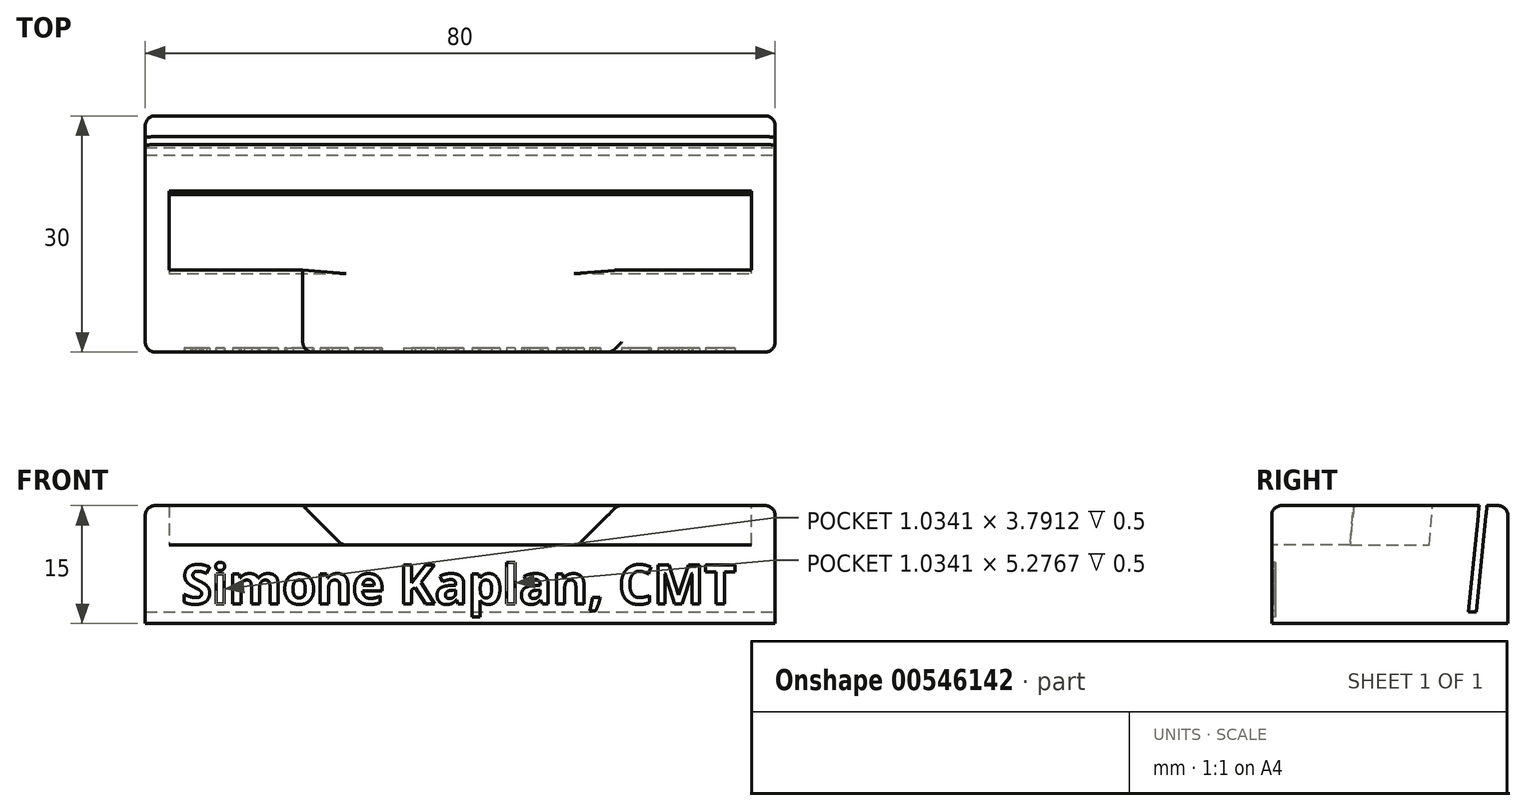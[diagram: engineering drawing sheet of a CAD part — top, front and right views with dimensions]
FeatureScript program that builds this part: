
annotation { "Feature Type Name" : "Feature", "Feature Type Description" : "" }
export const myFeature = defineFeature(function(context is Context, id is Id, definition is map)
    precondition{}
    {
        {
            var Q0;
            Q0=qCreatedBy(makeId("Right.planeOp"),FACE);
            var sketch = newSketch(context, id + "F0", { "sketchPlane" : qUnion([Q0])});
            skLineSegment(sketch, "E0.bottom", {"start": v(0, 0) * mm, "end": v(30, 0) * mm});
            skLineSegment(sketch, "E0.top", {"start": v(0, 15) * mm, "end": v(30, 15) * mm});
            skLineSegment(sketch, "E0.left", {"start": v(0, 0) * mm, "end": v(0, 15) * mm});
            skLineSegment(sketch, "E0.right", {"start": v(30, 0) * mm, "end": v(30, 15) * mm});
            skSolve(sketch);
        }
        {
            var Q0;
            Q0=qSketchRegion(id+"F0",true);
            extrude(context, id + "F1", {"entities" : qUnion([Q0]), "depth" : 80 * mm});
        }
        {
            var Q0;
            Q0=makeQuery(id+"F1.opExtrude","CAP_FACE",FACE,{"disambiguationData":[OSD([sQuery(id+"F0.wireOp",EDGE,"E0.bottom"),sQuery(id+"F0.wireOp",EDGE,"E0.top"),sQuery(id+"F0.wireOp",EDGE,"E0.left"),sQuery(id+"F0.wireOp",EDGE,"E0.right")])],"isStart":false});
            var sketch = newSketch(context, id + "F2", { "sketchPlane" : qUnion([Q0])});
            skLineSegment(sketch, "E1", {"start": v(10.42, 15) * mm, "end": v(9.98, 10) * mm});
            skLineSegment(sketch, "E2", {"start": v(9.98, 10) * mm, "end": v(20.02, 10) * mm});
            skLineSegment(sketch, "E3", {"start": v(20.02, 10) * mm, "end": v(20.46, 15) * mm});
            skPoint(sketch, "E4", {"position": v(15, 10) * mm});
            skLineSegment(sketch, "E5", {"start": v(26.98, 21.28) * mm, "end": v(25, 1.5) * mm});
            skLineSegment(sketch, "E6", {"start": v(25, 1.5) * mm, "end": v(26, 1.5) * mm});
            skLineSegment(sketch, "E7", {"start": v(26, 1.5) * mm, "end": v(27.99, 21.28) * mm});
            skLineSegment(sketch, "E8", {"start": v(26.98, 21.28) * mm, "end": v(27.99, 21.28) * mm});
            skSolve(sketch);
        }
        {
            var Q0;
            {var subQ0=sQuery(id+"F2.wireOp",EDGE,"E1");Q0=makeQuery(id+"F2.imprint","IMPRINT",FACE,{"disambiguationData":[TD([[makeQuery(id+"F2.imprint","IMPRINT",EDGE,{"derivedFrom":subQ0}),1.0]])]});}
            var Q1;
            Q1=makeQuery(id+"F2.imprint","IMPRINT",FACE,{"disambiguationData":[TD([[makeQuery(id+"F2.imprint","IMPRINT",EDGE,{"derivedFrom":sQuery(id+"F2.wireOp",EDGE,"E5")}),1.0]])]});
            extrude(context, id + "F3", {"entities" : qUnion([Q0, Q1]), "operationType" : NewBodyOperationType.REMOVE, "oppositeDirection" : true, "depth" : 80 * mm, "offsetDistance" : 25 * mm});
        }
        {
            var Q0;
            Q0=makeQuery(id+"F1.opExtrude","SWEPT_FACE",FACE,{"disambiguationData":[OSD([sQuery(id+"F0.wireOp",EDGE,"E0.left")])]});
            var sketch = newSketch(context, id + "F4", { "sketchPlane" : qUnion([Q0])});
            skLineSegment(sketch, "E9", {"start": v(20, 15) * mm, "end": v(25, 10) * mm});
            skLineSegment(sketch, "E10", {"start": v(25, 10) * mm, "end": v(55, 10) * mm});
            skLineSegment(sketch, "E11", {"start": v(55, 10) * mm, "end": v(60, 15) * mm});
            skLineSegment(sketch, "E12", {"start": v(60, 15) * mm, "end": v(20, 15) * mm});
            skPoint(sketch, "E13", {"position": v(40, 10) * mm});
            skPoint(sketch, "E14", {"position": v(40, 0) * mm});
            skSolve(sketch);
        }
        {
            var Q0;
            Q0=qSketchRegion(id+"F4",true);
            var Q1;
            Q1=makeQuery(id+"F3.boolean.opBoolean","COPY",FACE,{"derivedFrom":makeQuery(id+"F3.opExtrude","SWEPT_FACE",FACE,{"disambiguationData":[OSD([sQuery(id+"F2.wireOp",EDGE,"E3")])]})});
            extrude(context, id + "F5", {"entities" : qUnion([Q0]), "operationType" : NewBodyOperationType.REMOVE, "endBound" : BoundingType.UP_TO_SURFACE, "oppositeDirection" : true, "endBoundEntityFace" : qUnion([Q1]), "depth" : 23.7 * mm, "offsetDistance" : 25 * mm});
        }
        {
            var Q0;
            Q0=makeQuery(id+"F1.opExtrude","CAP_FACE",FACE,{"disambiguationData":[OSD([sQuery(id+"F0.wireOp",EDGE,"E0.bottom"),sQuery(id+"F0.wireOp",EDGE,"E0.top"),sQuery(id+"F0.wireOp",EDGE,"E0.left"),sQuery(id+"F0.wireOp",EDGE,"E0.right")])],"isStart":false});
            var sketch = newSketch(context, id + "F6", { "sketchPlane" : qUnion([Q0])});
            skLineSegment(sketch, "E15", {"start": v(20.46, 15) * mm, "end": v(10.42, 15) * mm});
            skLineSegment(sketch, "E16", {"start": v(10.42, 15) * mm, "end": v(9.98, 10) * mm});
            skLineSegment(sketch, "E17", {"start": v(9.98, 10) * mm, "end": v(20.02, 10) * mm});
            skLineSegment(sketch, "E18", {"start": v(20.02, 10) * mm, "end": v(20.46, 15) * mm});
            skSolve(sketch);
        }
        {
            var Q0;
            Q0=qSketchRegion(id+"F6",true);
            extrude(context, id + "F7", {"entities" : qUnion([Q0]), "operationType" : NewBodyOperationType.ADD, "oppositeDirection" : true, "depth" : 3 * mm, "offsetDistance" : 25 * mm});
        }
        {
            var Q0;
            Q0=qSketchRegion(id+"F6",true);
            extrude(context, id + "F8", {"entities" : qUnion([Q0]), "operationType" : NewBodyOperationType.ADD, "oppositeDirection" : true, "depth" : 80 * mm, "offsetDistance" : 25 * mm, "hasSecondDirection" : true, "secondDirectionOppositeDirection" : true, "secondDirectionDepth" : 77 * mm});
        }
        {
            var Q0;
            Q0=makeQuery(id+"F1.opExtrude","SWEPT_FACE",FACE,{"disambiguationData":[OSD([sQuery(id+"F0.wireOp",EDGE,"E0.left")])]});
            var sketch = newSketch(context, id + "F9", { "sketchPlane" : qUnion([Q0])});
            skText(sketch, "E19", { "text": "Simone Kaplan, CMT", "fontName": "OpenSans-Bold.ttf"});
            const initialGuessF9  = {"E19": [0.00463, 0.0025, 1, 0, 0.005]};
            skSetInitialGuess(sketch, initialGuessF9);
            skSolve(sketch);
        }
        {
            var Q0;
            Q0 = qSketchRegion(id + "F9", true);
            extrude(context, id + "F10", {"entities" : qUnion([Q0]), "operationType" : NewBodyOperationType.REMOVE, "oppositeDirection" : true, "depth" : 0.5 * mm, "offsetDistance" : 25 * mm});
        }
        {
            var Q0;
            {var subQ0=sQuery(id+"F0.wireOp",EDGE,"E0.left");var subQ1=sQuery(id+"F0.wireOp",EDGE,"E0.top");Q0=makeQuery(id+"F5.boolean.opBoolean","SPLIT",EDGE,{"disambiguationData":[TD([makeQuery(id+"F5.opExtrude","SWEPT_FACE",FACE,{"disambiguationData":[OSD([sQuery(id+"F4.wireOp",EDGE,"E9")])]})])],"derivedFrom":makeQuery(id+"F1.opExtrude","SWEPT_EDGE",EDGE,{"disambiguationData":[OSD([subQ1,subQ0])]})});}
            var Q1;
            {var subQ0=sQuery(id+"F0.wireOp",EDGE,"E0.left");var subQ1=sQuery(id+"F0.wireOp",EDGE,"E0.top");var subQ4=makeQuery(id+"F1.opExtrude","CAP_EDGE",EDGE,{"disambiguationData":[OSD([subQ1])],"isStart":true});Q1=makeQuery(id+"F8.boolean.opBoolean","MERGE",EDGE,{"derivedFrom":[makeQuery(id+"F3.boolean.opBoolean","SPLIT",EDGE,{"disambiguationData":[TD([makeQuery(id+"F1.opExtrude","SWEPT_FACE",FACE,{"disambiguationData":[OSD([subQ0])]})])],"derivedFrom":subQ4}),makeQuery(id+"F3.boolean.opBoolean","SPLIT",EDGE,{"disambiguationData":[TD([makeQuery(id+"F3.opExtrude","SWEPT_FACE",FACE,{"disambiguationData":[OSD([sQuery(id+"F2.wireOp",EDGE,"E3")])]})])],"derivedFrom":subQ4}),makeQuery(id+"F8.opExtrude","CAP_EDGE",EDGE,{"disambiguationData":[OSD([sQuery(id+"F6.wireOp",EDGE,"E15")])],"isStart":false})]});}
            var Q2;
            Q2=makeQuery(id+"F1.opExtrude","CAP_EDGE",EDGE,{"disambiguationData":[OSD([sQuery(id+"F0.wireOp",EDGE,"E0.left")])],"isStart":true});
            var Q3;
            Q3=makeQuery(id+"F1.opExtrude","CAP_EDGE",EDGE,{"disambiguationData":[OSD([sQuery(id+"F0.wireOp",EDGE,"E0.left")])],"isStart":false});
            var Q4;
            Q4=makeQuery(id+"F1.opExtrude","CAP_EDGE",EDGE,{"disambiguationData":[OSD([sQuery(id+"F0.wireOp",EDGE,"E0.right")])],"isStart":false});
            var Q5;
            Q5=makeQuery(id+"F5.boolean.opBoolean","COPY",EDGE,{"derivedFrom":makeQuery(id+"F5.opExtrude","SWEPT_EDGE",EDGE,{"disambiguationData":[OSD([sQuery(id+"F0.wireOp",EDGE,"E0.top"),sQuery(id+"F0.wireOp",EDGE,"E0.left"),sQuery(id+"F4.wireOp",EDGE,"E9"),sQuery(id+"F4.wireOp",EDGE,"E12")])]})});
            var Q6;
            Q6=makeQuery(id+"F5.boolean.opBoolean","COPY",EDGE,{"derivedFrom":makeQuery(id+"F5.opExtrude","CAP_EDGE",EDGE,{"disambiguationData":[OSD([sQuery(id+"F4.wireOp",EDGE,"E9")])],"isStart":true})});
            var Q7;
            {var subQ0=sQuery(id+"F0.wireOp",EDGE,"E0.left");var subQ1=sQuery(id+"F0.wireOp",EDGE,"E0.top");Q7=makeQuery(id+"F5.boolean.opBoolean","SPLIT",EDGE,{"disambiguationData":[TD([makeQuery(id+"F5.opExtrude","SWEPT_FACE",FACE,{"disambiguationData":[OSD([sQuery(id+"F4.wireOp",EDGE,"E11")])]})])],"derivedFrom":makeQuery(id+"F1.opExtrude","SWEPT_EDGE",EDGE,{"disambiguationData":[OSD([subQ1,subQ0])]})});}
            var Q8;
            {var subQ0=sQuery(id+"F0.wireOp",EDGE,"E0.left");var subQ1=sQuery(id+"F0.wireOp",EDGE,"E0.top");var subQ4=makeQuery(id+"F1.opExtrude","CAP_EDGE",EDGE,{"disambiguationData":[OSD([subQ1])],"isStart":false});Q8=makeQuery(id+"F7.boolean.opBoolean","MERGE",EDGE,{"derivedFrom":[makeQuery(id+"F3.boolean.opBoolean","SPLIT",EDGE,{"disambiguationData":[TD([makeQuery(id+"F1.opExtrude","SWEPT_FACE",FACE,{"disambiguationData":[OSD([subQ0])]})])],"derivedFrom":subQ4}),makeQuery(id+"F3.boolean.opBoolean","SPLIT",EDGE,{"disambiguationData":[TD([makeQuery(id+"F3.opExtrude","SWEPT_FACE",FACE,{"disambiguationData":[OSD([sQuery(id+"F2.wireOp",EDGE,"E3")])]})])],"derivedFrom":subQ4}),makeQuery(id+"F7.opExtrude","CAP_EDGE",EDGE,{"disambiguationData":[OSD([sQuery(id+"F6.wireOp",EDGE,"E15")])],"isStart":true})]});}
            var Q9;
            {var subQ0=sQuery(id+"F0.wireOp",EDGE,"E0.right");var subQ1=sQuery(id+"F0.wireOp",EDGE,"E0.top");Q9=makeQuery(id+"F3.boolean.opBoolean","SPLIT",EDGE,{"disambiguationData":[TD([makeQuery(id+"F1.opExtrude","SWEPT_FACE",FACE,{"disambiguationData":[OSD([subQ0])]})])],"derivedFrom":makeQuery(id+"F1.opExtrude","CAP_EDGE",EDGE,{"disambiguationData":[OSD([subQ1])],"isStart":false})});}
            var Q10;
            {var subQ0=sQuery(id+"F0.wireOp",EDGE,"E0.right");var subQ1=sQuery(id+"F0.wireOp",EDGE,"E0.top");Q10=makeQuery(id+"F3.boolean.opBoolean","SPLIT",EDGE,{"disambiguationData":[TD([makeQuery(id+"F1.opExtrude","SWEPT_FACE",FACE,{"disambiguationData":[OSD([subQ0])]})])],"derivedFrom":makeQuery(id+"F1.opExtrude","CAP_EDGE",EDGE,{"disambiguationData":[OSD([subQ1])],"isStart":true})});}
            var Q11;
            Q11=makeQuery(id+"F1.opExtrude","CAP_EDGE",EDGE,{"disambiguationData":[OSD([sQuery(id+"F0.wireOp",EDGE,"E0.right")])],"isStart":true});
            var Q12;
            Q12=makeQuery(id+"F1.opExtrude","SWEPT_EDGE",EDGE,{"disambiguationData":[OSD([sQuery(id+"F0.wireOp",EDGE,"E0.top"),sQuery(id+"F0.wireOp",EDGE,"E0.right")])]});
            var Q13;
            Q13=makeQuery(id+"F5.boolean.opBoolean","COPY",EDGE,{"derivedFrom":makeQuery(id+"F5.opExtrude","CAP_EDGE",EDGE,{"disambiguationData":[OSD([sQuery(id+"F4.wireOp",EDGE,"E11")])],"isStart":true})});
            var Q14;
            Q14=makeQuery(id+"F5.boolean.opBoolean","COPY",EDGE,{"derivedFrom":makeQuery(id+"F5.opExtrude","CAP_EDGE",EDGE,{"disambiguationData":[OSD([sQuery(id+"F4.wireOp",EDGE,"E10")])],"isStart":true})});
            var Q15;
            Q15=makeQuery(id+"F5.boolean.opBoolean","COPY",EDGE,{"derivedFrom":makeQuery(id+"F5.opExtrude","SWEPT_EDGE",EDGE,{"disambiguationData":[OSD([sQuery(id+"F4.wireOp",EDGE,"E9"),sQuery(id+"F4.wireOp",EDGE,"E10")])]})});
            var Q16;
            Q16=makeQuery(id+"F5.boolean.opBoolean","COPY",EDGE,{"derivedFrom":makeQuery(id+"F5.opExtrude","SWEPT_EDGE",EDGE,{"disambiguationData":[OSD([sQuery(id+"F4.wireOp",EDGE,"E10"),sQuery(id+"F4.wireOp",EDGE,"E11")])]})});
            var Q17;
            Q17=makeQuery(id+"F5.boolean.opBoolean","COPY",EDGE,{"derivedFrom":makeQuery(id+"F5.opExtrude","SWEPT_EDGE",EDGE,{"disambiguationData":[OSD([sQuery(id+"F0.wireOp",EDGE,"E0.top"),sQuery(id+"F0.wireOp",EDGE,"E0.left"),sQuery(id+"F4.wireOp",EDGE,"E11"),sQuery(id+"F4.wireOp",EDGE,"E12")])]})});
            fillet(context, id + "F11", {"entities" : qUnion([Q0, Q1, Q2, Q3, Q4, Q5, Q6, Q7, Q8, Q9, Q10, Q11, Q12, Q13, Q14, Q15, Q16, Q17]), "radius" : 1.25 * mm, "tangentPropagation" : true, "allowEdgeOverflow" : false});
        }
    });
